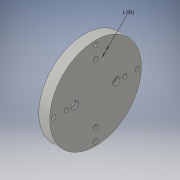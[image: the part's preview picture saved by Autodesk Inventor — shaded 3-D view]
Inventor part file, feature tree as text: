
AUTODESK INVENTOR PART (.ipt)
format: ipt  version: 2016 (Build 200138000, 138)  size: 315,392 bytes
history: native  units: in
note: dims shown in document units (in); Inventor stores cm internally (conversion verified against a paired STEP export)
features: sketch x6, extrude x3, revolve x1
ambient origin geometry x8: Origin, YZ Plane, XZ Plane, XY Plane, X Axis, Y Axis, Z Axis, Center Point
bodies: Solid1 (feature_tree)
feature tree (10):
  revolve  "Revolution1"  [1 undecoded]
  extrude  "Extrusion1"  Depth=0.105in
  sketch  "Sketch3"  dims[d4=0.105in d5=0.255in]
  sketch  "Sketch4"  dims[d6=0.2in d7=0.1in]
  extrude  "Extrusion2"  Depth=0.105in
  sketch  "Sketch5"  dims[d8=90.0deg]
  extrude  "Extrusion4"  Depth=0.1in
  sketch  "Sketch1"  dims[d0=1.2499in d1=0.3in]
  sketch  "Sketch2"  dims[d2=0.22in d3=0.105in]
  sketch  "Sketch8"  dims[d9=0.1181in d10=1.5748in d12=360.0deg d14=0.5in d15=0.0in d16=0.255in d17=0.1275in d18=0.1181in d19=1.5748in d21=360.0deg d23=0.2in d24=0.0in d25=1.14in d26=0.787in d42=1.0in d43=0.0in]
note: 1 required parameter value undecoded (feature->parameter linkage not recoverable at this tier; creation-order binding heuristic only, values carry confidence <= 0.55)
